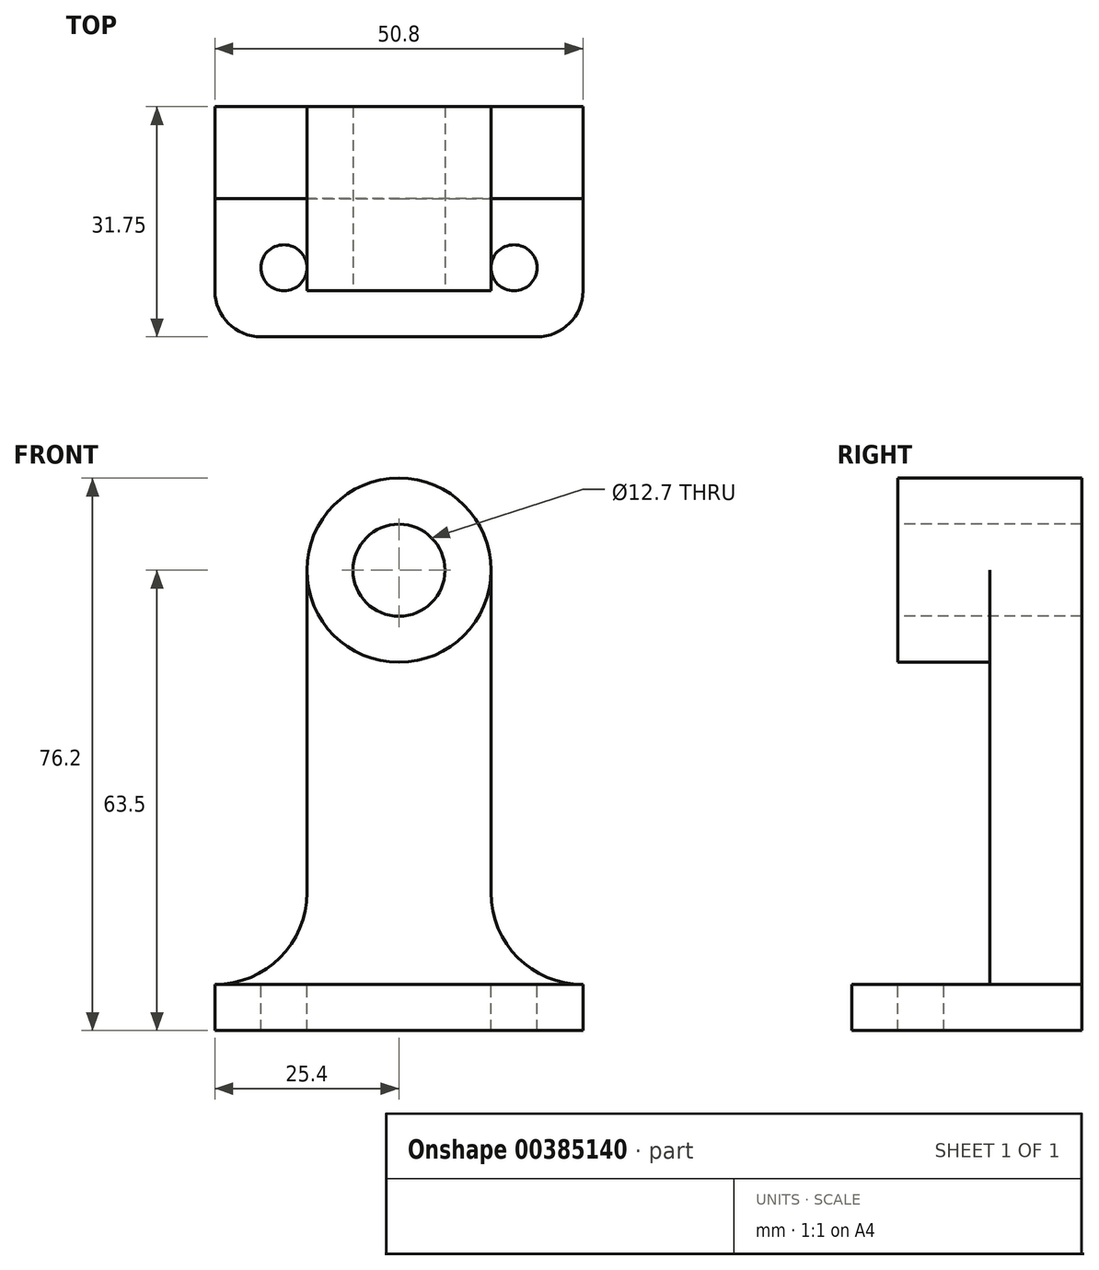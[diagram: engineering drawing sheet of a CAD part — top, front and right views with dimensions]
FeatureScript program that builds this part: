
annotation { "Feature Type Name" : "Feature", "Feature Type Description" : "" }
export const myFeature = defineFeature(function(context is Context, id is Id, definition is map)
    precondition{}
    {
        {
            var Q0;
            Q0=qCreatedBy(makeId("Right.planeOp"),FACE);
            var sketch = newSketch(context, id + "F0", { "sketchPlane" : qUnion([Q0])});
            skLineSegment(sketch, "E0", {"start": v(0, 0) * mm, "end": v(-31.75, 0) * mm});
            skLineSegment(sketch, "E1", {"start": v(-31.75, 0) * mm, "end": v(-31.75, 6.35) * mm});
            skLineSegment(sketch, "E2", {"start": v(-31.75, 6.35) * mm, "end": v(-12.7, 6.35) * mm});
            skLineSegment(sketch, "E3", {"start": v(-12.7, 6.35) * mm, "end": v(-12.7, 50.8) * mm});
            skLineSegment(sketch, "E4", {"start": v(-12.7, 50.8) * mm, "end": v(-25.4, 50.8) * mm});
            skLineSegment(sketch, "E5", {"start": v(-25.4, 50.8) * mm, "end": v(-25.4, 76.2) * mm});
            skLineSegment(sketch, "E6", {"start": v(-25.4, 76.2) * mm, "end": v(0, 76.2) * mm});
            skLineSegment(sketch, "E7", {"start": v(0, 76.2) * mm, "end": v(0, 0) * mm});
            skSolve(sketch);
        }
        {
            var Q0;
            Q0=makeQuery(id+"F0.imprint","IMPRINT",FACE,{"disambiguationData":[TD([[makeQuery(id+"F0.imprint","IMPRINT",EDGE,{"derivedFrom":sQuery(id+"F0.wireOp",EDGE,"E0")}),-1.0]])]});
            extrude(context, id + "F1", {"entities" : qUnion([Q0]), "depth" : 50.8 * mm});
        }
        {
            var Q0;
            Q0=makeQuery(id+"F1.opExtrude","SWEPT_FACE",FACE,{"disambiguationData":[OSD([sQuery(id+"F0.wireOp",EDGE,"E6")])]});
            var sketch = newSketch(context, id + "F2", { "sketchPlane" : qUnion([Q0])});
            skLineSegment(sketch, "E8", {"start": v(12.7, 0) * mm, "end": v(12.7, -25.4) * mm});
            skLineSegment(sketch, "E9", {"start": v(38.1, 0) * mm, "end": v(38.1, -25.4) * mm});
            skSolve(sketch);
        }
        {
            var Q0;
            {var subQ0=sQuery(id+"F2.wireOp",EDGE,"E8");Q0=makeQuery(id+"F2.imprint","IMPRINT",FACE,{"disambiguationData":[TD([[makeQuery(id+"F2.imprint","IMPRINT",EDGE,{"derivedFrom":subQ0}),-1.0]])]});}
            var Q1;
            {var subQ0=sQuery(id+"F2.wireOp",EDGE,"E9");Q1=makeQuery(id+"F2.imprint","IMPRINT",FACE,{"disambiguationData":[TD([[makeQuery(id+"F2.imprint","IMPRINT",EDGE,{"derivedFrom":subQ0}),1.0]])]});}
            extrude(context, id + "F3", {"entities" : qUnion([Q0, Q1]), "operationType" : NewBodyOperationType.REMOVE, "oppositeDirection" : true, "depth" : 69.85 * mm});
        }
        {
            var Q0;
            Q0=makeQuery(id+"F1.opExtrude","SWEPT_FACE",FACE,{"disambiguationData":[OSD([sQuery(id+"F0.wireOp",EDGE,"E5")])]});
            var sketch = newSketch(context, id + "F4", { "sketchPlane" : qUnion([Q0])});
            skCircle(sketch, "E10", {"center": v(25.4, 63.5) * mm, "radius": 12.7 * mm});
            skSolve(sketch);
        }
        {
            var Q0;
            {var subQ0=sQuery(id+"F4.wireOp",EDGE,"E10");var subQ1=sQuery(id+"F0.wireOp",EDGE,"E6");var subQ2=sQuery(id+"F0.wireOp",EDGE,"E5");var subQ3=makeQuery(id+"F1.opExtrude","SWEPT_EDGE",EDGE,{"disambiguationData":[OSD([subQ2,subQ1])]});var subQ4=makeQuery(id+"F4.imprint","INTERSECT",VERTEX,{"derivedFrom":[subQ3,subQ0]});Q0=makeQuery(id+"F4.imprint","IMPRINT",FACE,{"disambiguationData":[TD([[makeQuery(id+"F4.imprint","IMPRINT",EDGE,{"disambiguationData":[TD([[subQ4,-1.0]])],"derivedFrom":subQ0}),-1.0]])]});}
            var Q1;
            {var subQ0=sQuery(id+"F4.wireOp",EDGE,"E10");var subQ1=sQuery(id+"F0.wireOp",EDGE,"E6");var subQ2=sQuery(id+"F0.wireOp",EDGE,"E5");var subQ3=makeQuery(id+"F1.opExtrude","SWEPT_EDGE",EDGE,{"disambiguationData":[OSD([subQ2,subQ1])]});var subQ4=makeQuery(id+"F4.imprint","INTERSECT",VERTEX,{"derivedFrom":[subQ3,subQ0]});Q1=makeQuery(id+"F4.imprint","IMPRINT",FACE,{"disambiguationData":[TD([[makeQuery(id+"F4.imprint","IMPRINT",EDGE,{"disambiguationData":[TD([[subQ4,1.0]])],"derivedFrom":subQ0}),-1.0]])]});}
            var Q2;
            {var subQ0=sQuery(id+"F4.wireOp",EDGE,"E10");var subQ1=sQuery(id+"F0.wireOp",EDGE,"E5");var subQ4=makeQuery(id+"F1.opExtrude","SWEPT_EDGE",EDGE,{"disambiguationData":[OSD([sQuery(id+"F0.wireOp",EDGE,"E4"),subQ1])]});var subQ5=makeQuery(id+"F4.imprint","INTERSECT",VERTEX,{"derivedFrom":[subQ4,subQ0]});Q2=makeQuery(id+"F4.imprint","IMPRINT",FACE,{"disambiguationData":[TD([[makeQuery(id+"F4.imprint","IMPRINT",EDGE,{"disambiguationData":[TD([[subQ5,1.0]])],"derivedFrom":subQ0}),-1.0]])]});}
            var Q3;
            {var subQ0=sQuery(id+"F4.wireOp",EDGE,"E10");var subQ1=sQuery(id+"F0.wireOp",EDGE,"E5");var subQ4=makeQuery(id+"F1.opExtrude","SWEPT_EDGE",EDGE,{"disambiguationData":[OSD([sQuery(id+"F0.wireOp",EDGE,"E4"),subQ1])]});var subQ5=makeQuery(id+"F4.imprint","INTERSECT",VERTEX,{"derivedFrom":[subQ4,subQ0]});Q3=makeQuery(id+"F4.imprint","IMPRINT",FACE,{"disambiguationData":[TD([[makeQuery(id+"F4.imprint","IMPRINT",EDGE,{"disambiguationData":[TD([[subQ5,-1.0]])],"derivedFrom":subQ0}),-1.0]])]});}
            extrude(context, id + "F5", {"entities" : qUnion([Q0, Q1, Q2, Q3]), "operationType" : NewBodyOperationType.REMOVE, "oppositeDirection" : true, "depth" : 12.7 * mm});
        }
        {
            var Q0;
            Q0=makeQuery(id+"F5.boolean.opBoolean","COPY",FACE,{"derivedFrom":makeQuery(id+"F5.opExtrude","CAP_FACE",FACE,{"disambiguationData":[OSD([sQuery(id+"F0.wireOp",EDGE,"E5"),sQuery(id+"F0.wireOp",EDGE,"E6"),sQuery(id+"F2.wireOp",EDGE,"E8"),sQuery(id+"F4.wireOp",EDGE,"E10")])],"isStart":false})});
            var Q1;
            Q1=makeQuery(id+"F5.boolean.opBoolean","COPY",FACE,{"derivedFrom":makeQuery(id+"F5.opExtrude","CAP_FACE",FACE,{"disambiguationData":[OSD([sQuery(id+"F0.wireOp",EDGE,"E5"),sQuery(id+"F0.wireOp",EDGE,"E6"),sQuery(id+"F2.wireOp",EDGE,"E9"),sQuery(id+"F4.wireOp",EDGE,"E10")])],"isStart":false})});
            extrude(context, id + "F6", {"entities" : qUnion([Q0, Q1]), "operationType" : NewBodyOperationType.REMOVE, "oppositeDirection" : true, "depth" : 25.4 * mm});
        }
        {
            var Q0;
            Q0=makeQuery(id+"F1.opExtrude","SWEPT_FACE",FACE,{"disambiguationData":[OSD([sQuery(id+"F0.wireOp",EDGE,"E5")])]});
            var sketch = newSketch(context, id + "F7", { "sketchPlane" : qUnion([Q0])});
            skCircle(sketch, "E11", {"center": v(25.4, 63.5) * mm, "radius": 6.35 * mm});
            skSolve(sketch);
        }
        {
            var Q0;
            Q0=makeQuery(id+"F7.imprint","IMPRINT",FACE,{"disambiguationData":[TD([[makeQuery(id+"F7.imprint","IMPRINT",EDGE,{"derivedFrom":sQuery(id+"F7.wireOp",EDGE,"E11")}),1.0]])]});
            extrude(context, id + "F8", {"entities" : qUnion([Q0]), "operationType" : NewBodyOperationType.REMOVE, "oppositeDirection" : true, "depth" : 25.4 * mm});
        }
        {
            var Q0;
            Q0=makeQuery(id+"F3.boolean.opBoolean","COPY",FACE,{"derivedFrom":makeQuery(id+"F3.opExtrude","SWEPT_FACE",FACE,{"disambiguationData":[OSD([sQuery(id+"F2.wireOp",EDGE,"E8")])]})});
            var sketch = newSketch(context, id + "F9", { "sketchPlane" : qUnion([Q0])});
            skLineSegment(sketch, "E12", {"start": v(0, 19.05) * mm, "end": v(0, 6.35) * mm});
            skLineSegment(sketch, "E13", {"start": v(12.7, 19.05) * mm, "end": v(12.7, 6.35) * mm});
            skLineSegment(sketch, "E14", {"start": v(0, 19.05) * mm, "end": v(12.7, 19.05) * mm});
            skSolve(sketch);
        }
        {
            var Q0;
            Q0=makeQuery(id+"F9.imprint","IMPRINT",FACE,{"disambiguationData":[TD([[makeQuery(id+"F9.imprint","IMPRINT",EDGE,{"derivedFrom":sQuery(id+"F9.wireOp",EDGE,"E12")}),-1.0]])]});
            extrude(context, id + "F10", {"entities" : qUnion([Q0]), "operationType" : NewBodyOperationType.ADD, "depth" : 12.7 * mm});
        }
        {
            var Q0;
            Q0=makeQuery(id+"F3.boolean.opBoolean","COPY",FACE,{"derivedFrom":makeQuery(id+"F3.opExtrude","SWEPT_FACE",FACE,{"disambiguationData":[OSD([sQuery(id+"F2.wireOp",EDGE,"E9")])]})});
            var sketch = newSketch(context, id + "F11", { "sketchPlane" : qUnion([Q0])});
            skLineSegment(sketch, "E15", {"start": v(-12.7, 19.05) * mm, "end": v(-12.7, 6.35) * mm});
            skLineSegment(sketch, "E16", {"start": v(0, 19.05) * mm, "end": v(0, 6.35) * mm});
            skLineSegment(sketch, "E17", {"start": v(-12.7, 19.05) * mm, "end": v(0, 19.05) * mm});
            skSolve(sketch);
        }
        {
            var Q0;
            Q0=makeQuery(id+"F11.imprint","IMPRINT",FACE,{"disambiguationData":[TD([[makeQuery(id+"F11.imprint","IMPRINT",EDGE,{"derivedFrom":sQuery(id+"F11.wireOp",EDGE,"E15")}),1.0]])]});
            extrude(context, id + "F12", {"entities" : qUnion([Q0]), "operationType" : NewBodyOperationType.ADD, "depth" : 12.7 * mm});
        }
        {
            var Q0;
            {var subQ0=sQuery(id+"F4.wireOp",EDGE,"E10");var subQ1=sQuery(id+"F0.wireOp",EDGE,"E6");var subQ2=sQuery(id+"F0.wireOp",EDGE,"E5");var subQ3=sQuery(id+"F0.wireOp",EDGE,"E4");Q0=makeQuery(id+"F12.boolean.opBoolean","MERGE",FACE,{"derivedFrom":[makeQuery(id+"F10.boolean.opBoolean","MERGE",FACE,{"derivedFrom":[makeQuery(id+"F5.boolean.opBoolean","MERGE",FACE,{"derivedFrom":[makeQuery(id+"F1.opExtrude","SWEPT_FACE",FACE,{"disambiguationData":[OSD([sQuery(id+"F0.wireOp",EDGE,"E3")])]}),makeQuery(id+"F5.opExtrude","CAP_FACE",FACE,{"disambiguationData":[OSD([subQ3,subQ2,subQ1,sQuery(id+"F2.wireOp",EDGE,"E8"),subQ0])],"isStart":false}),makeQuery(id+"F5.opExtrude","CAP_FACE",FACE,{"disambiguationData":[OSD([subQ3,subQ2,subQ1,sQuery(id+"F2.wireOp",EDGE,"E9"),subQ0])],"isStart":false})]}),makeQuery(id+"F10.opExtrude","SWEPT_FACE",FACE,{"disambiguationData":[OSD([sQuery(id+"F9.wireOp",EDGE,"E13")])]})]}),makeQuery(id+"F12.opExtrude","SWEPT_FACE",FACE,{"disambiguationData":[OSD([sQuery(id+"F11.wireOp",EDGE,"E15")])]})]});}
            var sketch = newSketch(context, id + "F13", { "sketchPlane" : qUnion([Q0])});
            skCircle(sketch, "E18", {"center": v(0, 19.05) * mm, "radius": 12.7 * mm});
            skCircle(sketch, "E19", {"center": v(50.8, 19.05) * mm, "radius": 12.7 * mm});
            skSolve(sketch);
        }
        {
            var Q0;
            {var subQ1=sQuery(id+"F9.wireOp",EDGE,"E13");var subQ4=makeQuery(id+"F10.opExtrude","CAP_EDGE",EDGE,{"disambiguationData":[OSD([subQ1])],"isStart":false});Q0=makeQuery(id+"F13.imprint","IMPRINT",FACE,{"disambiguationData":[TD([[makeQuery(id+"F13.imprint","IMPRINT",EDGE,{"derivedFrom":subQ4}),1.0]])]});}
            var Q1;
            {var subQ1=sQuery(id+"F11.wireOp",EDGE,"E15");var subQ4=makeQuery(id+"F12.opExtrude","CAP_EDGE",EDGE,{"disambiguationData":[OSD([subQ1])],"isStart":false});Q1=makeQuery(id+"F13.imprint","IMPRINT",FACE,{"disambiguationData":[TD([[makeQuery(id+"F13.imprint","IMPRINT",EDGE,{"derivedFrom":subQ4}),-1.0]])]});}
            extrude(context, id + "F14", {"entities" : qUnion([Q0, Q1]), "operationType" : NewBodyOperationType.REMOVE, "oppositeDirection" : true, "depth" : 25.4 * mm});
        }
        {
            var Q0;
            {var subQ0=sQuery(id+"F0.wireOp",EDGE,"E7");var subQ1=sQuery(id+"F0.wireOp",EDGE,"E6");var subQ2=sQuery(id+"F0.wireOp",EDGE,"E5");Q0=makeQuery(id+"F3.boolean.opBoolean","MERGE",FACE,{"derivedFrom":[makeQuery(id+"F1.opExtrude","SWEPT_FACE",FACE,{"disambiguationData":[OSD([sQuery(id+"F0.wireOp",EDGE,"E2")])]}),makeQuery(id+"F3.opExtrude","CAP_FACE",FACE,{"disambiguationData":[OSD([subQ2,subQ1,subQ0,sQuery(id+"F2.wireOp",EDGE,"E8")])],"isStart":false}),makeQuery(id+"F3.opExtrude","CAP_FACE",FACE,{"disambiguationData":[OSD([subQ2,subQ1,subQ0,sQuery(id+"F2.wireOp",EDGE,"E9")])],"isStart":false})]});}
            var sketch = newSketch(context, id + "F15", { "sketchPlane" : qUnion([Q0])});
            skCircle(sketch, "E20", {"center": v(9.53, -22.23) * mm, "radius": 3.18 * mm});
            skCircle(sketch, "E21", {"center": v(41.28, -22.23) * mm, "radius": 3.18 * mm});
            skSolve(sketch);
        }
        {
            var Q0;
            Q0=makeQuery(id+"F15.imprint","IMPRINT",FACE,{"disambiguationData":[TD([[makeQuery(id+"F15.imprint","IMPRINT",EDGE,{"derivedFrom":sQuery(id+"F15.wireOp",EDGE,"E20")}),1.0]])]});
            var Q1;
            Q1=makeQuery(id+"F15.imprint","IMPRINT",FACE,{"disambiguationData":[TD([[makeQuery(id+"F15.imprint","IMPRINT",EDGE,{"derivedFrom":sQuery(id+"F15.wireOp",EDGE,"E21")}),1.0]])]});
            extrude(context, id + "F16", {"entities" : qUnion([Q0, Q1]), "operationType" : NewBodyOperationType.REMOVE, "oppositeDirection" : true, "depth" : 25.4 * mm});
        }
        {
            var Q0;
            {var subQ0=sQuery(id+"F0.wireOp",EDGE,"E7");var subQ1=sQuery(id+"F0.wireOp",EDGE,"E6");var subQ2=sQuery(id+"F0.wireOp",EDGE,"E5");Q0=makeQuery(id+"F3.boolean.opBoolean","MERGE",FACE,{"derivedFrom":[makeQuery(id+"F1.opExtrude","SWEPT_FACE",FACE,{"disambiguationData":[OSD([sQuery(id+"F0.wireOp",EDGE,"E2")])]}),makeQuery(id+"F3.opExtrude","CAP_FACE",FACE,{"disambiguationData":[OSD([subQ2,subQ1,subQ0,sQuery(id+"F2.wireOp",EDGE,"E8")])],"isStart":false}),makeQuery(id+"F3.opExtrude","CAP_FACE",FACE,{"disambiguationData":[OSD([subQ2,subQ1,subQ0,sQuery(id+"F2.wireOp",EDGE,"E9")])],"isStart":false})]});}
            var sketch = newSketch(context, id + "F17", { "sketchPlane" : qUnion([Q0])});
            skCircle(sketch, "E22", {"center": v(6.35, -25.4) * mm, "radius": 6.35 * mm});
            skCircle(sketch, "E23", {"center": v(44.45, -25.4) * mm, "radius": 6.35 * mm});
            skSolve(sketch);
        }
        {
            var Q0;
            {var subQ0=sQuery(id+"F17.wireOp",EDGE,"E22");var subQ2=sQuery(id+"F0.wireOp",EDGE,"E2");var subQ5=makeQuery(id+"F1.opExtrude","SWEPT_EDGE",EDGE,{"disambiguationData":[OSD([sQuery(id+"F0.wireOp",EDGE,"E1"),subQ2])]});var subQ6=makeQuery(id+"F17.imprint","INTERSECT",VERTEX,{"derivedFrom":[subQ5,subQ0]});Q0=makeQuery(id+"F17.imprint","IMPRINT",FACE,{"disambiguationData":[TD([[makeQuery(id+"F17.imprint","IMPRINT",EDGE,{"disambiguationData":[TD([[subQ6,1.0]])],"derivedFrom":subQ0}),-1.0]])]});}
            var Q1;
            {var subQ0=sQuery(id+"F17.wireOp",EDGE,"E23");var subQ2=sQuery(id+"F0.wireOp",EDGE,"E2");var subQ5=makeQuery(id+"F1.opExtrude","SWEPT_EDGE",EDGE,{"disambiguationData":[OSD([sQuery(id+"F0.wireOp",EDGE,"E1"),subQ2])]});var subQ6=makeQuery(id+"F17.imprint","INTERSECT",VERTEX,{"derivedFrom":[subQ5,subQ0]});Q1=makeQuery(id+"F17.imprint","IMPRINT",FACE,{"disambiguationData":[TD([[makeQuery(id+"F17.imprint","IMPRINT",EDGE,{"disambiguationData":[TD([[subQ6,-1.0]])],"derivedFrom":subQ0}),-1.0]])]});}
            extrude(context, id + "F18", {"entities" : qUnion([Q0, Q1]), "operationType" : NewBodyOperationType.REMOVE, "oppositeDirection" : true, "depth" : 25.4 * mm});
        }
    });
